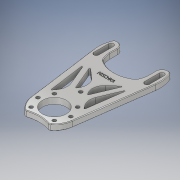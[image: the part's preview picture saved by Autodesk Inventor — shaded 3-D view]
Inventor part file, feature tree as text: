
AUTODESK INVENTOR PART (.ipt)
format: ipt  version: 2019.3 (Build 233278000, 278)  size: 685,056 bytes
history: native  units: mm
features: thread x7, emboss x2, fillet x2, sketch x2, extrude x1, chamfer x1, other x1
ambient origin geometry x8: Origin, YZ Plane, XZ Plane, XY Plane, X Axis, Y Axis, Z Axis, Center Point
bodies: Body1 (feature_tree)
feature tree (16):
  extrude  "Extrusion3"  Depth=20.0mm
  thread  "Thread1"  [1 undecoded]
  thread  "Thread2"  [1 undecoded]
  thread  "Thread3"  [1 undecoded]
  thread  "Thread4"  [1 undecoded]
  thread  "Thread5"  [1 undecoded]
  thread  "Thread6"  [1 undecoded]
  thread  "Thread7"  [1 undecoded]
  emboss  "Emboss1"
  emboss  "Emboss2"
  fillet  "Fillet3"  Radius=3.0mm
  fillet  "Fillet5"  Radius=3.0mm
  chamfer  "Chamfer3"  Distance=3.0mm
  other  "Center Lines"
  sketch  "Sketch1"  dims[d0=62.5mm d1=20.0mm d3=3.5mm d4=3.5mm d5=7.0mm d7=43.0mm d9=3.5mm d11=32.0mm d15=4.0mm d24=3.0mm d25=3.0mm]
  sketch  "Sketch3"  dims[d27=45.0deg d29=3.0mm d30=3.0mm d31=22.0mm d40=5.0mm d41=0.0mm d44=10.0mm d45=0.0mm d46=10.0mm d47=0.0mm d48=10.0mm d49=0.0mm d50=20.0mm d51=52.0mm d53=26.0mm d54=10.0mm d55=0.0mm d56=10.0mm d57=0.0mm d58=10.0mm d59=0.0mm d60=10.0mm d61=0.0mm d65=0.2mm d66=0.0mm d69=5.0mm d70=15.0mm d71=5.0mm d72=15.0mm d73=0.2mm d74=0.0mm d75=91.463203mm d76=7.5mm d77=3.75mm d78=1.0mm d81=6.25mm d82=12.5mm d85=5.0mm d86=4.0mm d91=0.5mm d94=2.0mm d95=0.5mm d96=2.0mm d97=45.0deg d98=15.0deg d99=24.0mm d101=28.0mm d102=28.0mm]
note: 7 required parameter values undecoded (feature->parameter linkage not recoverable at this tier; creation-order binding heuristic only, values carry confidence <= 0.55)
